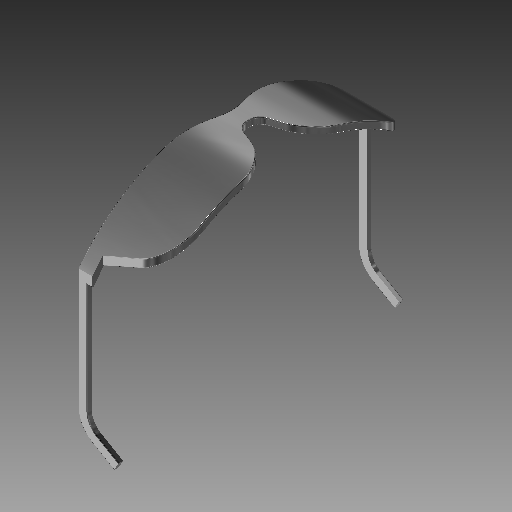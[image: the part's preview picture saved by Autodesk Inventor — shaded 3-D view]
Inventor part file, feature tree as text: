
AUTODESK INVENTOR PART (.ipt)
format: ipt  version: 2022 (Build 260153000, 153)  size: 500,736 bytes
history: native  units: mm (DEFAULTED — no unit token found)
features: fillet x4, extrude x3, sketch x3, mirror x2, other x1, projected_geometry x1
ambient origin geometry x8: Origin, YZ Plane, XZ Plane, XY Plane, X Axis, Y Axis, Z Axis, Center Point
bodies: Solid1 (feature_tree)
feature tree (14):
  other  "iMan - 2D BODY"
  extrude  "Extrusion1"  Depth=10.0mm
  mirror  "Mirror1"
  extrude  "Extrusion2"  Depth=48.490708mm
  fillet  "Fillet1"  Radius=96.981416mm
  extrude  "Extrusion3"  Depth=12.7mm
  fillet  "Fillet2"  Radius=96.981416mm
  mirror  "Mirror2"
  fillet  "Fillet3"  Radius=116.3777mm
  fillet  "Fillet4"  Radius=4.7625mm
  sketch  "Sketch2"  dims[d1=10.0mm d16=3.490659mm]
  sketch  "Sketch3"  dims[d17=6.35mm d18=48.490708mm d19=96.981416mm]
  projected_geometry  "Projected Loop1"
  sketch  "Sketch4"  dims[d20=19.396283mm d21=24.245354mm d22=96.981416mm d23=0.0mm d24=116.3777mm d25=4.7625mm d26=25.4mm d27=0.0mm d29=6.303792mm d30=92.363254mm d31=30.0deg d32=3.175mm d33=0.0mm d34=19.05mm d35=1.5875mm d36=0.79375mm d37=27.708976mm d39=9.698142mm d40=15.0deg d43=7.273606mm d55=12.7mm d56=25.4mm d57=7.112mm d58=25.4mm d59=76.2mm]
